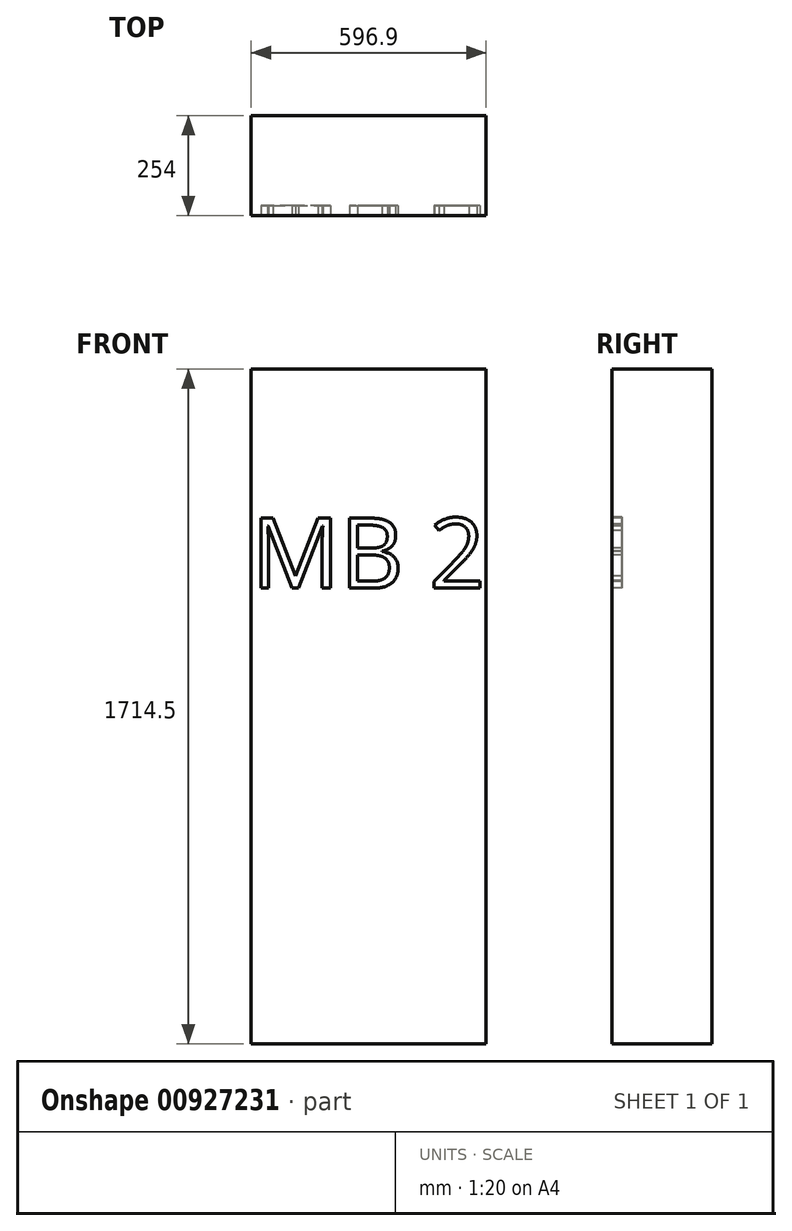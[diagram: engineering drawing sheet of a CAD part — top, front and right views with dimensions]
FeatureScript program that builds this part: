
annotation { "Feature Type Name" : "Feature", "Feature Type Description" : "" }
export const myFeature = defineFeature(function(context is Context, id is Id, definition is map)
    precondition{}
    {
        {
            var Q0;
            Q0=qCreatedBy(makeId("Front.planeOp"),FACE);
            var sketch = newSketch(context, id + "F0", { "sketchPlane" : qUnion([Q0])});
            skLineSegment(sketch, "E0.bottom", {"start": v(298.45, -857.25) * mm, "end": v(-298.45, -857.25) * mm});
            skLineSegment(sketch, "E0.top", {"start": v(298.45, 857.25) * mm, "end": v(-298.45, 857.25) * mm});
            skLineSegment(sketch, "E0.left", {"start": v(298.45, -857.25) * mm, "end": v(298.45, 857.25) * mm});
            skLineSegment(sketch, "E0.right", {"start": v(-298.45, -857.25) * mm, "end": v(-298.45, 857.25) * mm});
            skPoint(sketch, "E0.middle", {"position": v(0, 0) * mm});
            skSolve(sketch);
        }
        {
            var Q0;
            Q0 = qSketchRegion(id + "F0", true);
            extrude(context, id + "F1", {"entities" : qUnion([Q0]), "endBound" : BoundingType.SYMMETRIC, "depth" : 254 * mm, "offsetDistance" : 25.4 * mm});
        }
        {
            var Q0;
            Q0=makeQuery(id+"F1.opExtrude","CAP_FACE",FACE,{"disambiguationData":[OSD([sQuery(id+"F0.wireOp",EDGE,"E0.bottom"),sQuery(id+"F0.wireOp",EDGE,"E0.top"),sQuery(id+"F0.wireOp",EDGE,"E0.left"),sQuery(id+"F0.wireOp",EDGE,"E0.right")])],"isStart":false});
            var sketch = newSketch(context, id + "F2", { "sketchPlane" : qUnion([Q0])});
            skText(sketch, "E1", { "text": "MB 2", "fontName": "OpenSans-Regular.ttf"});
            const initialGuessF2  = {"E1": [-0.29845, 0.3006, 1, 0, 0.17955]};
            skSetInitialGuess(sketch, initialGuessF2);
            skSolve(sketch);
        }
        {
            var Q0;
            Q0 = qSketchRegion(id + "F2", true);
            extrude(context, id + "F3", {"entities" : qUnion([Q0]), "operationType" : NewBodyOperationType.REMOVE, "oppositeDirection" : true, "depth" : 25.4 * mm, "offsetDistance" : 25.4 * mm});
        }
    });
